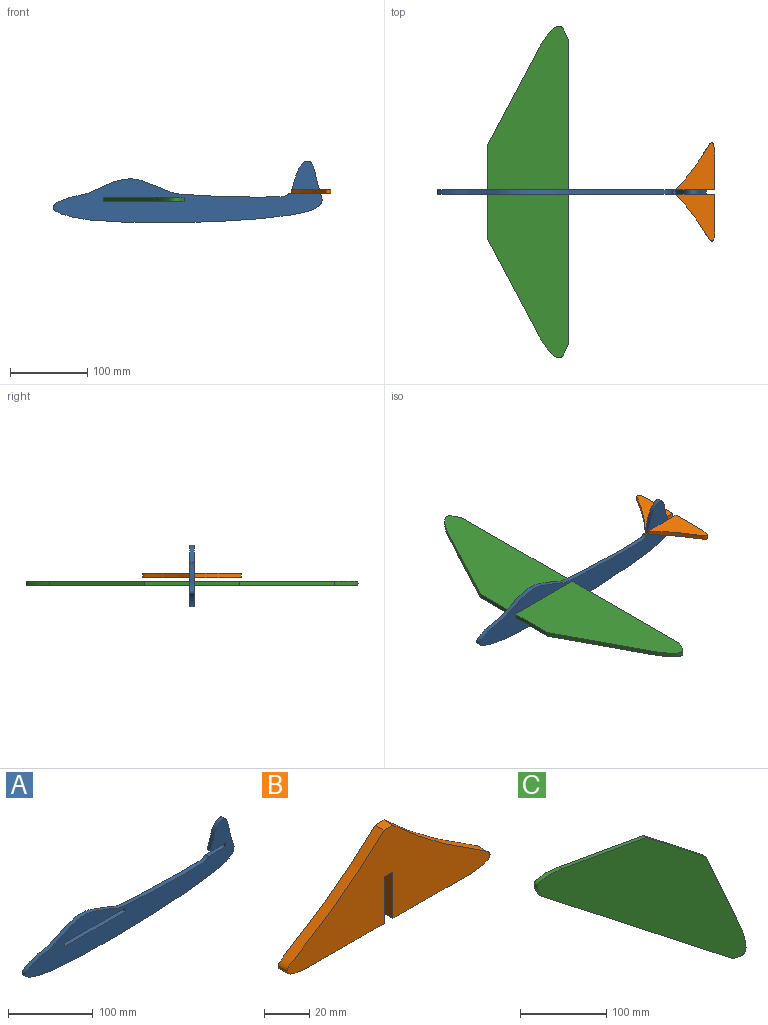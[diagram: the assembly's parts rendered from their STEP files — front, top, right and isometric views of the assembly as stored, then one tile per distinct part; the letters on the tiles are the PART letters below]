
ASSEMBLY  parts=3 mates=2
PART A: 10 faces, bbox 355.4x5.6x85.6 mm
  f0: plane 101.6x5.59mm, normal (0,0,-1), area 567.7mm2, adj f1,f7,f8,f9
  f1: plane 5.59x5.59mm, normal (-1,0,0), area 31.2mm2, adj f0,f2,f8,f9
  f2: plane 101.6x5.59mm, normal (0,0,1), area 567.7mm2, adj f1,f7,f8,f9
  f3: plane 5.59x5.59mm, normal (-1,0,0), area 31.2mm2, adj f4,f6,f8,f9
  f4: plane 28.69x5.59mm, normal (0,0,1), area 160.3mm2, adj f3,f5,f8,f9
  f5: extruded ~344.28x79.89mm, area 4224.1mm2, adj f4,f6,f8,f9
  f6: plane 25.4x5.59mm, normal (0,0,-1), area 141.9mm2, adj f3,f5,f8,f9
  f7: plane 5.59x5.59mm, normal (1,0,0), area 31.2mm2, adj f0,f2,f8,f9
  f8: plane 355.39x85.64mm, normal (0,-1,0), area 12512.2mm2, adj f0,f1,f2,f3,f4,f5,f6,f7
  f9: plane 355.39x85.64mm, normal (0,1,0), area 12512.2mm2, adj f0,f1,f2,f3,f4,f5,f6,f7
PART B: 10 faces, bbox 128.9x5.6x50.8 mm
  f0: plane 49.04x5.59mm, normal (0,0,-1), area 274mm2, adj f1,f7,f8,f9
  f1: extruded ~60.9x50.79mm, area 505.2mm2, adj f0,f2,f8,f9
  f2: plane 5.59x5.59mm, normal (0,0,1), area 31.2mm2, adj f1,f3,f8,f9
  f3: extruded ~60.95x50.79mm, area 511.9mm2, adj f2,f4,f8,f9
  f4: plane 47.8x5.59mm, normal (0,0,-1), area 267.1mm2, adj f3,f5,f8,f9
  f5: plane 25.4x5.59mm, normal (1,0,0), area 141.9mm2, adj f4,f6,f8,f9
  f6: plane 5.59x5.59mm, normal (0,0,-1), area 31.2mm2, adj f5,f7,f8,f9
  f7: plane 25.4x5.59mm, normal (-1,0,0), area 141.9mm2, adj f0,f6,f8,f9
  f8: plane 128.91x50.79mm, normal (0,-1,0), area 3369.5mm2, adj f0,f1,f2,f3,f4,f5,f6,f7
  f9: plane 128.91x50.79mm, normal (0,1,0), area 3369.5mm2, adj f0,f1,f2,f3,f4,f5,f6,f7
PART C: 8 faces, bbox 345.3x5.6x275.7 mm
  f0: plane 311.72x244.18mm, normal (-0.62,0,-0.79), area 2212.7mm2, adj f1,f5,f6,f7
  f1: extruded ~41.61x22.7mm, area 354.1mm2, adj f0,f2,f6,f7
  f2: plane 128.08x56.9mm, normal (0.91,0,0.41), area 783.1mm2, adj f1,f3,f6,f7
  f3: plane 96.72x75.77mm, normal (0.62,0,0.79), area 686.6mm2, adj f2,f4,f6,f7
  f4: plane 137.98x24.58mm, normal (0.18,0,0.98), area 783.1mm2, adj f3,f5,f6,f7
  f5: extruded ~41.2x24.53mm, area 354.1mm2, adj f0,f4,f6,f7
  f6: plane 345.28x275.74mm, normal (0,-1,0), area 32013.5mm2, adj f0,f1,f2,f3,f4,f5
  f7: plane 345.28x275.74mm, normal (0,1,0), area 32013.5mm2, adj f0,f1,f2,f3,f4,f5
PLACE A t=(-76.27,57.1,-125.26)mm
PLACE B rot(axis=(0.58,-0.58,-0.58),120deg) t=(443.38,164.15,51.74)mm
PLACE C rot(axis=(-0.33,-0.67,0.67),143.9deg) t=(331.71,1.2,36.03)mm
MATE fastened B.f6 <-> A.f3  axis (1,0,0) through (282,54.31,48.94)mm
MATE fastened C.f3 <-> A.f7  axis (-1,0,0) through (12.63,54.31,38.82)mm
